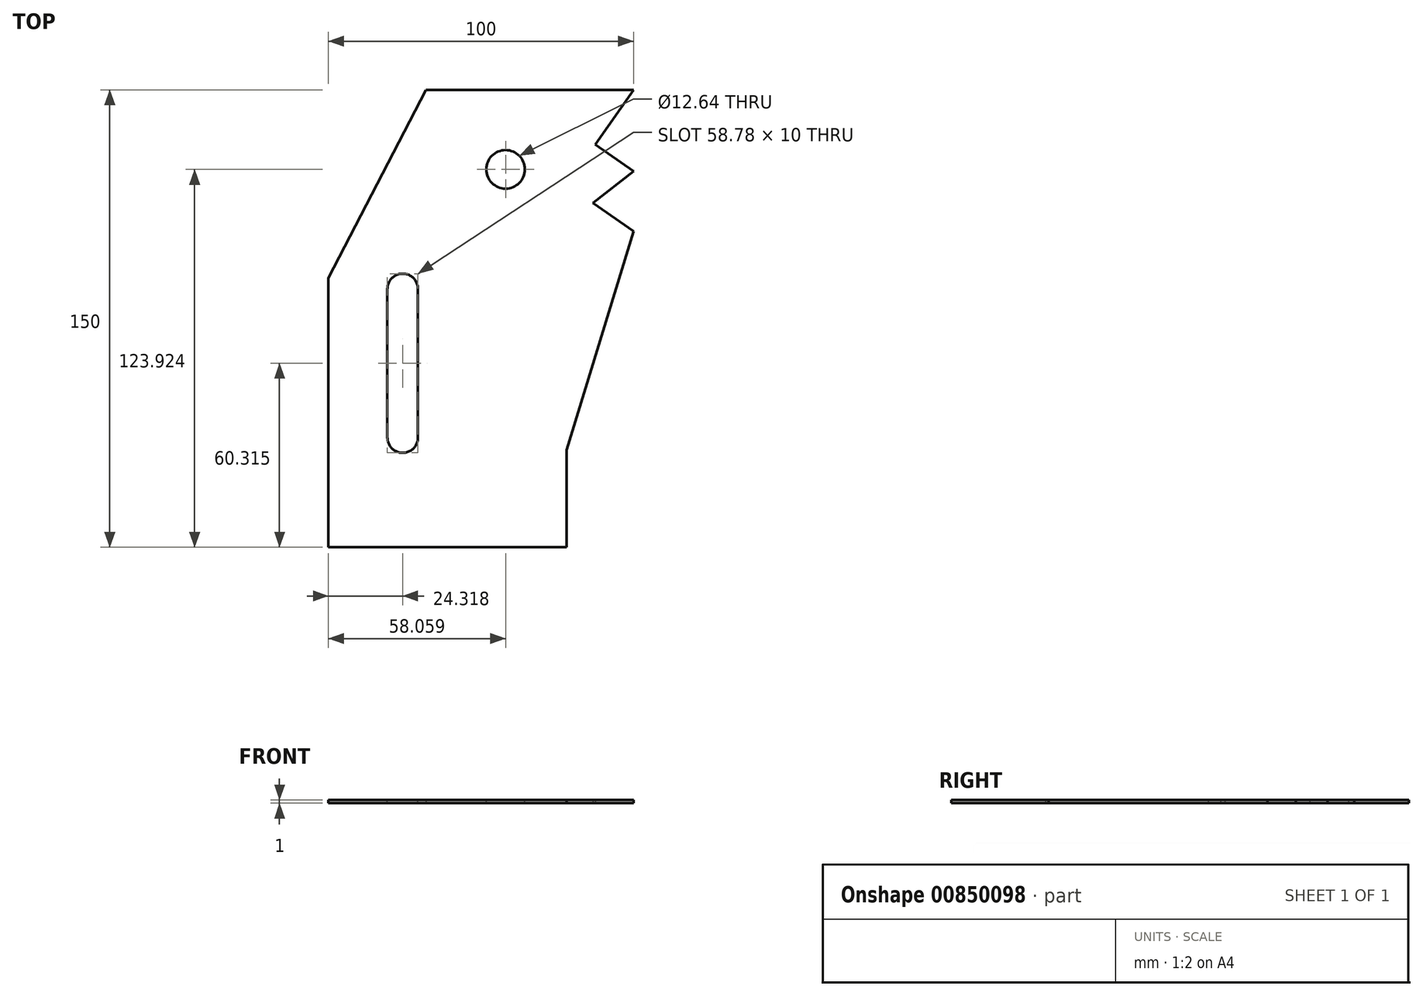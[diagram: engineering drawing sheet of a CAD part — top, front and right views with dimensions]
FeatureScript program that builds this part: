
annotation { "Feature Type Name" : "Feature", "Feature Type Description" : "" }
export const myFeature = defineFeature(function(context is Context, id is Id, definition is map)
    precondition{}
    {
        {
            var Q0;
            Q0=qCreatedBy(makeId("Top.planeOp"),FACE);
            var sketch = newSketch(context, id + "F0", { "sketchPlane" : qUnion([Q0])});
            skLineSegment(sketch, "E0.bottom", {"start": v(-18.06, 75) * mm, "end": v(50, 75) * mm});
            skLineSegment(sketch, "E0.top", {"start": v(-50, -75) * mm, "end": v(28.1, -75) * mm});
            skLineSegment(sketch, "E0.left", {"start": v(-50, 13.22) * mm, "end": v(-50, -75) * mm});
            skPoint(sketch, "E0.middle", {"position": v(0, 0) * mm});
            skLineSegment(sketch, "E1", {"start": v(-50, 13.22) * mm, "end": v(-18.06, 75) * mm});
            skLineSegment(sketch, "E2", {"start": v(50, 75) * mm, "end": v(37.49, 57.03) * mm});
            skLineSegment(sketch, "E3", {"start": v(37.49, 57.03) * mm, "end": v(50, 48.31) * mm});
            skLineSegment(sketch, "E4", {"start": v(50, 48.31) * mm, "end": v(36.7, 37.86) * mm});
            skLineSegment(sketch, "E5", {"start": v(36.7, 37.86) * mm, "end": v(50, 28.6) * mm});
            skLineSegment(sketch, "E6", {"start": v(50, 28.6) * mm, "end": v(28.1, -43.11) * mm});
            skLineSegment(sketch, "E7", {"start": v(28.1, -43.11) * mm, "end": v(28.1, -75) * mm});
            skPoint(sketch, "E8.orphan", {"position": v(-50, 75) * mm});
            skPoint(sketch, "E9.orphan", {"position": v(50, -75) * mm});
            skSolve(sketch);
        }
        {
            var Q0;
            Q0=qSketchRegion(id+"F0",true);
            extrude(context, id + "F1", {"entities" : qUnion([Q0]), "depth" : 1 * mm, "offsetDistance" : 25 * mm});
        }
        {
            var Q0;
            Q0=makeQuery(id+"F1.opExtrude","CAP_FACE",FACE,{"disambiguationData":[OSD([sQuery(id+"F0.wireOp",EDGE,"E0.bottom"),sQuery(id+"F0.wireOp",EDGE,"E0.top"),sQuery(id+"F0.wireOp",EDGE,"E0.left"),sQuery(id+"F0.wireOp",EDGE,"E1"),sQuery(id+"F0.wireOp",EDGE,"E2"),sQuery(id+"F0.wireOp",EDGE,"E3"),sQuery(id+"F0.wireOp",EDGE,"E4"),sQuery(id+"F0.wireOp",EDGE,"E5"),sQuery(id+"F0.wireOp",EDGE,"E6"),sQuery(id+"F0.wireOp",EDGE,"E7")])],"isStart":false});
            var sketch = newSketch(context, id + "F2", { "sketchPlane" : qUnion([Q0])});
            skCircle(sketch, "E10", {"center": v(8.06, 48.92) * mm, "radius": 6.32 * mm});
            skArc(sketch, "E11", {"start": v(-20.7, 9.24) * mm, "mid": v(-25.45, 14.7) * mm, "end": v(-30.68, 9.71) * mm});
            skArc(sketch, "E12", {"start": v(-30.68, -39.08) * mm, "mid": v(-25.68, -44.08) * mm, "end": v(-20.68, -39.07) * mm});
            skLineSegment(sketch, "E13", {"start": v(-20.7, 10.19) * mm, "end": v(-20.68, -39.07) * mm});
            skLineSegment(sketch, "E14", {"start": v(-30.68, 9.71) * mm, "end": v(-30.68, -39.08) * mm});
            skSolve(sketch);
        }
        {
            var Q0;
            Q0=qSketchRegion(id+"F2",true);
            extrude(context, id + "F3", {"entities" : qUnion([Q0]), "operationType" : NewBodyOperationType.REMOVE, "oppositeDirection" : true, "depth" : 25 * mm, "offsetDistance" : 25 * mm});
        }
    });
